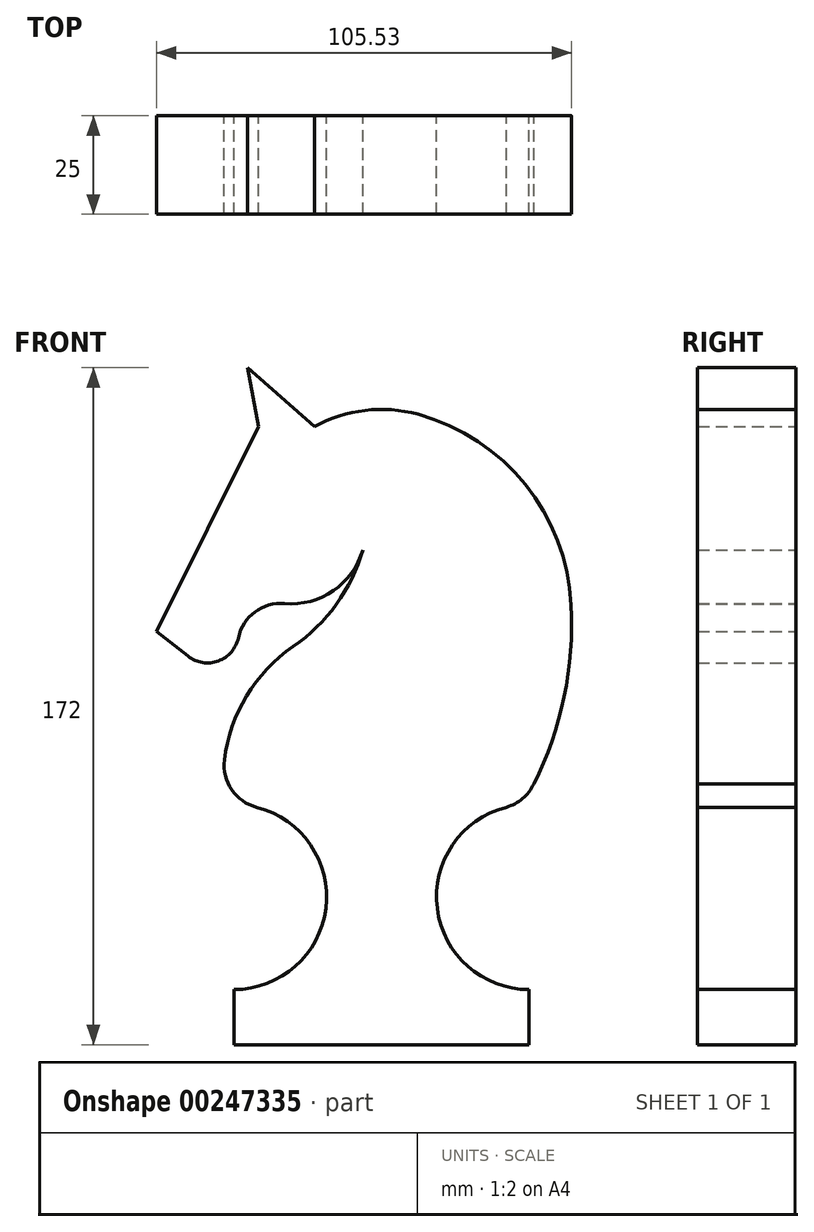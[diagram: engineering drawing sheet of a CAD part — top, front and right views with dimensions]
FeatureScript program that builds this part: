
annotation { "Feature Type Name" : "Feature", "Feature Type Description" : "" }
export const myFeature = defineFeature(function(context is Context, id is Id, definition is map)
    precondition{}
    {
        {
            var Q0;
            Q0=qCreatedBy(makeId("Front.planeOp"),FACE);
            var sketch = newSketch(context, id + "F0", { "sketchPlane" : qUnion([Q0])});
            skLineSegment(sketch, "E0", {"start": v(-37.5, 0) * mm, "end": v(37.5, 0) * mm});
            skLineSegment(sketch, "E1", {"start": v(-37.5, 0) * mm, "end": v(-37.5, 14) * mm});
            skArc(sketch, "E2", {"start": v(-37.5, 14) * mm, "mid": v(-14.15, 34.61) * mm, "end": v(-31.7, 60.34) * mm});
            skArc(sketch, "E3", {"start": v(-39.92, 72.33) * mm, "mid": v(-38.08, 64.79) * mm, "end": v(-31.7, 60.34) * mm});
            skLineSegment(sketch, "E4", {"start": v(0, -10.92) * mm, "end": v(0, 215.33) * mm, "construction": true});
            skArc(sketch, "E5", {"start": v(-49.14, 98.7) * mm, "mid": v(-41.47, 97.49) * mm, "end": v(-36.39, 103.36) * mm});
            skArc(sketch, "E6", {"start": v(-24.66, 112.07) * mm, "mid": v(-32.18, 109.95) * mm, "end": v(-36.39, 103.36) * mm});
            skArc(sketch, "E7", {"start": v(-24.66, 112.07) * mm, "mid": v(-12.25, 115.33) * mm, "end": v(-4.75, 125.73) * mm});
            skArc(sketch, "E8.MirrorC", {"start": v(39.23, 67.65) * mm, "mid": v(36.4, 63.04) * mm, "end": v(31.7, 60.34) * mm});
            skArc(sketch, "E9.MirrorC", {"start": v(37.5, 14) * mm, "mid": v(14.15, 34.61) * mm, "end": v(31.7, 60.34) * mm});
            skLineSegment(sketch, "E10.MirrorCS", {"start": v(37.5, 0) * mm, "end": v(37.5, 14) * mm});
            skLineSegment(sketch, "E11", {"start": v(-49.14, 98.7) * mm, "end": v(-57.22, 105) * mm});
            skLineSegment(sketch, "E12", {"start": v(-57.22, 105) * mm, "end": v(-31.26, 157) * mm});
            skArc(sketch, "E13", {"start": v(-22.47, 101.14) * mm, "mid": v(-11.47, 111.9) * mm, "end": v(-4.75, 125.73) * mm});
            skArc(sketch, "E14", {"start": v(-22.47, 101.14) * mm, "mid": v(-34.29, 88.61) * mm, "end": v(-39.92, 72.33) * mm});
            skLineSegment(sketch, "E15", {"start": v(-31.26, 157) * mm, "end": v(-34, 172) * mm});
            skLineSegment(sketch, "E16", {"start": v(-34, 172) * mm, "end": v(-17, 157) * mm});
            skArc(sketch, "E17", {"start": v(9.23, 160.17) * mm, "mid": v(-4.2, 161.15) * mm, "end": v(-17, 157) * mm});
            skArc(sketch, "E18", {"start": v(31.52, 60.3) * mm, "mid": v(35.65, 62.38) * mm, "end": v(38.56, 65.99) * mm});
            skLineSegment(sketch, "E19", {"start": v(46.66, 121.93) * mm, "end": v(94.3, 121.93) * mm, "construction": true});
            skLineSegment(sketch, "E20", {"start": v(-4.75, 125.73) * mm, "end": v(-4.75, 82.6) * mm, "construction": true});
            skArc(sketch, "E21.trimOffspring", {"start": v(48.19, 111.76) * mm, "mid": v(33.44, 145.8) * mm, "end": v(0, 161.83) * mm});
            skArc(sketch, "E22.trimOffspring", {"start": v(38.45, 65.77) * mm, "mid": v(47.24, 93.16) * mm, "end": v(47.1, 121.93) * mm});
            skSolve(sketch);
        }
        {
            var Q0;
            Q0 = qSketchRegion(id + "F0", true);
            extrude(context, id + "F1", {"entities" : qUnion([Q0]), "depth" : 25 * mm});
        }
    });
